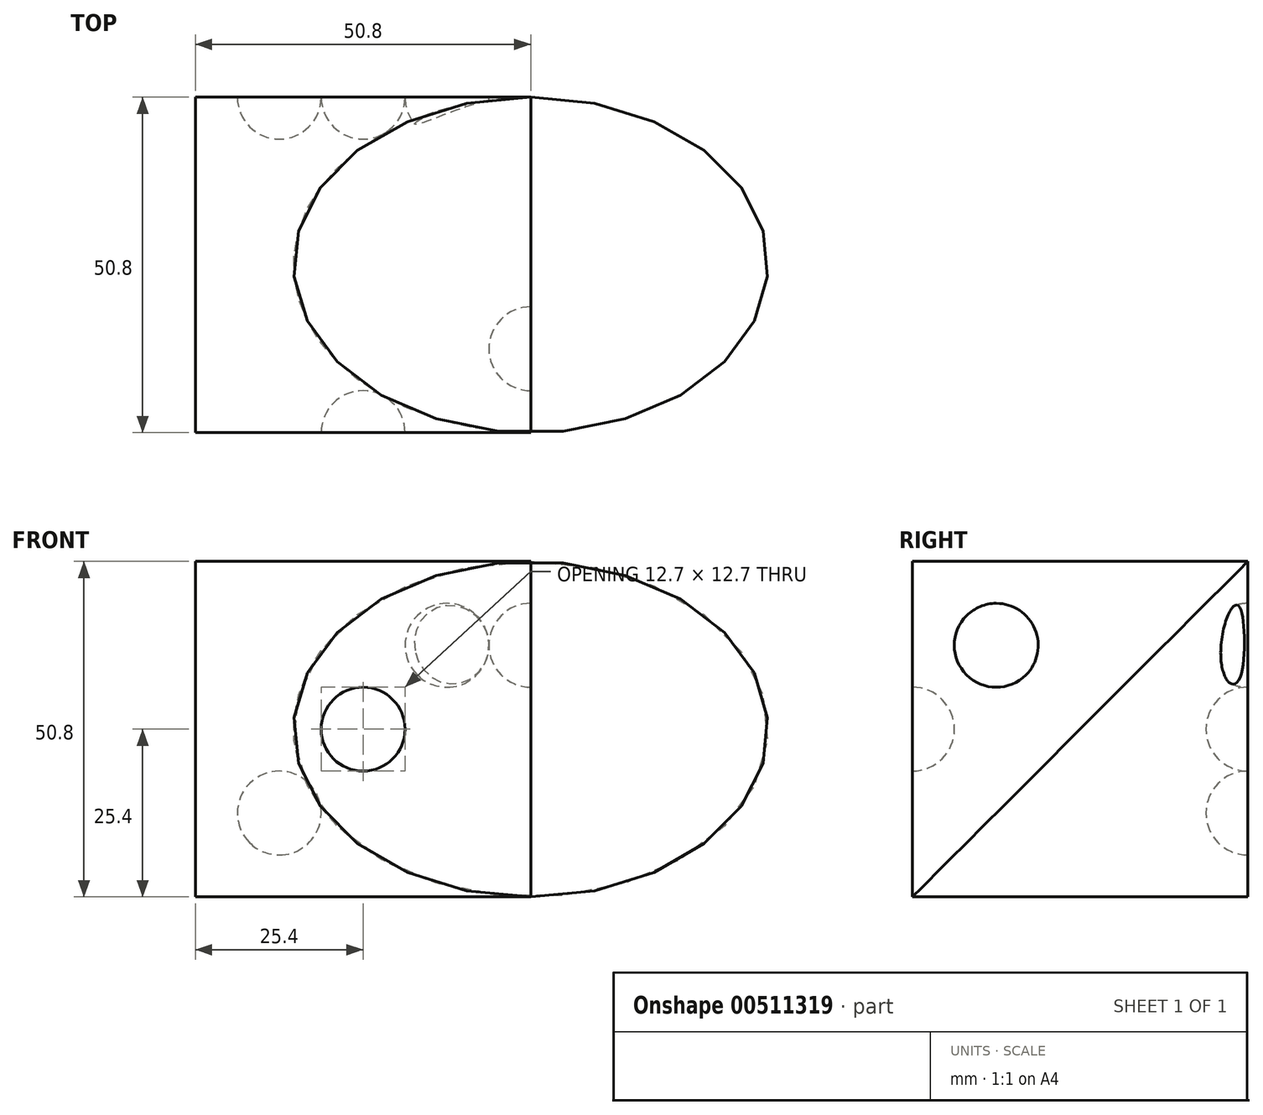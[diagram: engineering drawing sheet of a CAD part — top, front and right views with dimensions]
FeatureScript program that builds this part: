
annotation { "Feature Type Name" : "Feature", "Feature Type Description" : "" }
export const myFeature = defineFeature(function(context is Context, id is Id, definition is map)
    precondition{}
    {
        {
            var Q0;
            Q0=qCreatedBy(makeId("Front.planeOp"),FACE);
            var sketch = newSketch(context, id + "F0", { "sketchPlane" : qUnion([Q0])});
            skLineSegment(sketch, "E0.bottom", {"start": v(0, 0) * mm, "end": v(50.8, 0) * mm});
            skLineSegment(sketch, "E0.top", {"start": v(0, 50.8) * mm, "end": v(50.8, 50.8) * mm});
            skLineSegment(sketch, "E0.left", {"start": v(0, 0) * mm, "end": v(0, 50.8) * mm});
            skLineSegment(sketch, "E0.right", {"start": v(50.8, 0) * mm, "end": v(50.8, 50.8) * mm});
            skLineSegment(sketch, "E1", {"start": v(50.8, 2.1) * mm, "end": v(53, 0) * mm});
            skPoint(sketch, "E2.center.orphan", {"position": v(26.5, 25.4) * mm});
            skSolve(sketch);
        }
        {
            var Q0;
            {var subQ1=sQuery(id+"F0.wireOp",EDGE,"E0.bottom");Q0=makeQuery(id+"F0.imprint","IMPRINT",FACE,{"disambiguationData":[TD([[makeQuery(id+"F0.imprint","IMPRINT",EDGE,{"derivedFrom":subQ1}),1.0]])]});}
            extrude(context, id + "F1", {"entities" : qUnion([Q0]), "depth" : 50.8 * mm, "offsetDistance" : 25.4 * mm});
        }
        {
            var Q0;
            Q0=makeQuery(id+"F1.opExtrude","SWEPT_FACE",FACE,{"disambiguationData":[OSD([sQuery(id+"F0.wireOp",EDGE,"E0.right")])]});
            var sketch = newSketch(context, id + "F2", { "sketchPlane" : qUnion([Q0])});
            skLineSegment(sketch, "E3", {"start": v(-50.8, 50.8) * mm, "end": v(0, 0) * mm});
            skCircle(sketch, "E4", {"center": v(-38.1, 38.1) * mm, "radius": 6.35 * mm});
            skCircle(sketch, "E5", {"center": v(-12.7, 12.7) * mm, "radius": 6.35 * mm});
            skSolve(sketch);
        }
        {
            var Q0;
            {var subQ0=sQuery(id+"F2.wireOp",EDGE,"E4");var subQ1=sQuery(id+"F2.wireOp",EDGE,"E3");var subQ2=makeQuery(id+"F2.imprint","INTERSECT",VERTEX,{"disambiguationData":[OD(0.0)],"derivedFrom":[subQ1,subQ0]});Q0=makeQuery(id+"F2.imprint","IMPRINT",FACE,{"disambiguationData":[TD([[makeQuery(id+"F2.imprint","IMPRINT",EDGE,{"disambiguationData":[TD([[subQ2,-1.0]])],"derivedFrom":subQ1}),1.0]])]});}
            var Q1;
            {var subQ0=sQuery(id+"F2.wireOp",EDGE,"E5");var subQ1=sQuery(id+"F2.wireOp",EDGE,"E3");var subQ2=makeQuery(id+"F2.imprint","INTERSECT",VERTEX,{"disambiguationData":[OD(0.0)],"derivedFrom":[subQ1,subQ0]});Q1=makeQuery(id+"F2.imprint","IMPRINT",FACE,{"disambiguationData":[TD([[makeQuery(id+"F2.imprint","IMPRINT",EDGE,{"disambiguationData":[TD([[subQ2,-1.0]])],"derivedFrom":subQ1}),1.0]])]});}
            var Q2;
            Q2=sQuery(id+"F2.wireOp",EDGE,"E3");
            revolve(context, id + "F3", {"operationType" : NewBodyOperationType.REMOVE, "entities" : qUnion([Q0, Q1]), "axis" : qUnion([Q2]), "revolveType" : RevolveType.FULL, "oppositeDirection" : true});
        }
        {
            var Q0;
            Q0=makeQuery(id+"F1.opExtrude","CAP_FACE",FACE,{"disambiguationData":[OSD([sQuery(id+"F0.wireOp",EDGE,"E0.bottom"),sQuery(id+"F0.wireOp",EDGE,"E0.top"),sQuery(id+"F0.wireOp",EDGE,"E0.left"),sQuery(id+"F0.wireOp",EDGE,"E0.right")])],"isStart":false});
            var sketch = newSketch(context, id + "F4", { "sketchPlane" : qUnion([Q0])});
            skCircle(sketch, "E6", {"center": v(25.4, 25.4) * mm, "radius": 6.35 * mm});
            skPoint(sketch, "E7.orphan", {"position": v(0, 50.8) * mm});
            skPoint(sketch, "E8.end.orphan", {"position": v(50.8, 0) * mm});
            skLineSegment(sketch, "E9", {"start": v(25.4, 50.8) * mm, "end": v(25.4, 0) * mm});
            skSolve(sketch);
        }
        {
            var Q0;
            {var subQ0=sQuery(id+"F4.wireOp",EDGE,"E9");var subQ1=sQuery(id+"F4.wireOp",EDGE,"E6");var subQ2=makeQuery(id+"F4.imprint","INTERSECT",VERTEX,{"disambiguationData":[OD(0.0)],"derivedFrom":[subQ1,subQ0]});Q0=makeQuery(id+"F4.imprint","IMPRINT",FACE,{"disambiguationData":[TD([[makeQuery(id+"F4.imprint","IMPRINT",EDGE,{"disambiguationData":[TD([[subQ2,-1.0]])],"derivedFrom":subQ1}),1.0]])]});}
            var Q1;
            Q1=sQuery(id+"F4.wireOp",EDGE,"E9");
            revolve(context, id + "F5", {"operationType" : NewBodyOperationType.REMOVE, "entities" : qUnion([Q0]), "axis" : qUnion([Q1]), "revolveType" : RevolveType.FULL, "oppositeDirection" : true});
        }
        {
            var Q0;
            Q0=makeQuery(id+"F1.opExtrude","CAP_FACE",FACE,{"disambiguationData":[OSD([sQuery(id+"F0.wireOp",EDGE,"E0.bottom"),sQuery(id+"F0.wireOp",EDGE,"E0.top"),sQuery(id+"F0.wireOp",EDGE,"E0.left"),sQuery(id+"F0.wireOp",EDGE,"E0.right")])],"isStart":true});
            var sketch = newSketch(context, id + "F6", { "sketchPlane" : qUnion([Q0])});
            skLineSegment(sketch, "E10", {"start": v(-50.8, 50.8) * mm, "end": v(0, 0) * mm});
            skCircle(sketch, "E11", {"center": v(-25.4, 25.4) * mm, "radius": 6.35 * mm});
            skCircle(sketch, "E12", {"center": v(-12.7, 12.7) * mm, "radius": 6.35 * mm});
            skCircle(sketch, "E13", {"center": v(-38.1, 38.1) * mm, "radius": 6.35 * mm});
            skSolve(sketch);
        }
        {
            var Q0;
            {var subQ0=sQuery(id+"F6.wireOp",EDGE,"E12");var subQ1=sQuery(id+"F6.wireOp",EDGE,"E10");var subQ2=makeQuery(id+"F6.imprint","INTERSECT",VERTEX,{"disambiguationData":[OD(0.0)],"derivedFrom":[subQ1,subQ0]});Q0=makeQuery(id+"F6.imprint","IMPRINT",FACE,{"disambiguationData":[TD([[makeQuery(id+"F6.imprint","IMPRINT",EDGE,{"disambiguationData":[TD([[subQ2,-1.0]])],"derivedFrom":subQ1}),1.0]])]});}
            var Q1;
            {var subQ0=sQuery(id+"F6.wireOp",EDGE,"E11");var subQ1=sQuery(id+"F6.wireOp",EDGE,"E10");var subQ2=makeQuery(id+"F6.imprint","INTERSECT",VERTEX,{"disambiguationData":[OD(0.0)],"derivedFrom":[subQ1,subQ0]});Q1=makeQuery(id+"F6.imprint","IMPRINT",FACE,{"disambiguationData":[TD([[makeQuery(id+"F6.imprint","IMPRINT",EDGE,{"disambiguationData":[TD([[subQ2,-1.0]])],"derivedFrom":subQ1}),1.0]])]});}
            var Q2;
            {var subQ0=sQuery(id+"F6.wireOp",EDGE,"E13");var subQ1=sQuery(id+"F6.wireOp",EDGE,"E10");var subQ2=makeQuery(id+"F6.imprint","INTERSECT",VERTEX,{"disambiguationData":[OD(0.0)],"derivedFrom":[subQ1,subQ0]});Q2=makeQuery(id+"F6.imprint","IMPRINT",FACE,{"disambiguationData":[TD([[makeQuery(id+"F6.imprint","IMPRINT",EDGE,{"disambiguationData":[TD([[subQ2,-1.0]])],"derivedFrom":subQ1}),1.0]])]});}
            var Q3;
            Q3=sQuery(id+"F6.wireOp",EDGE,"E10");
            revolve(context, id + "F7", {"operationType" : NewBodyOperationType.REMOVE, "entities" : qUnion([Q0, Q1, Q2]), "axis" : qUnion([Q3]), "revolveType" : RevolveType.FULL, "oppositeDirection" : true});
        }
    });
